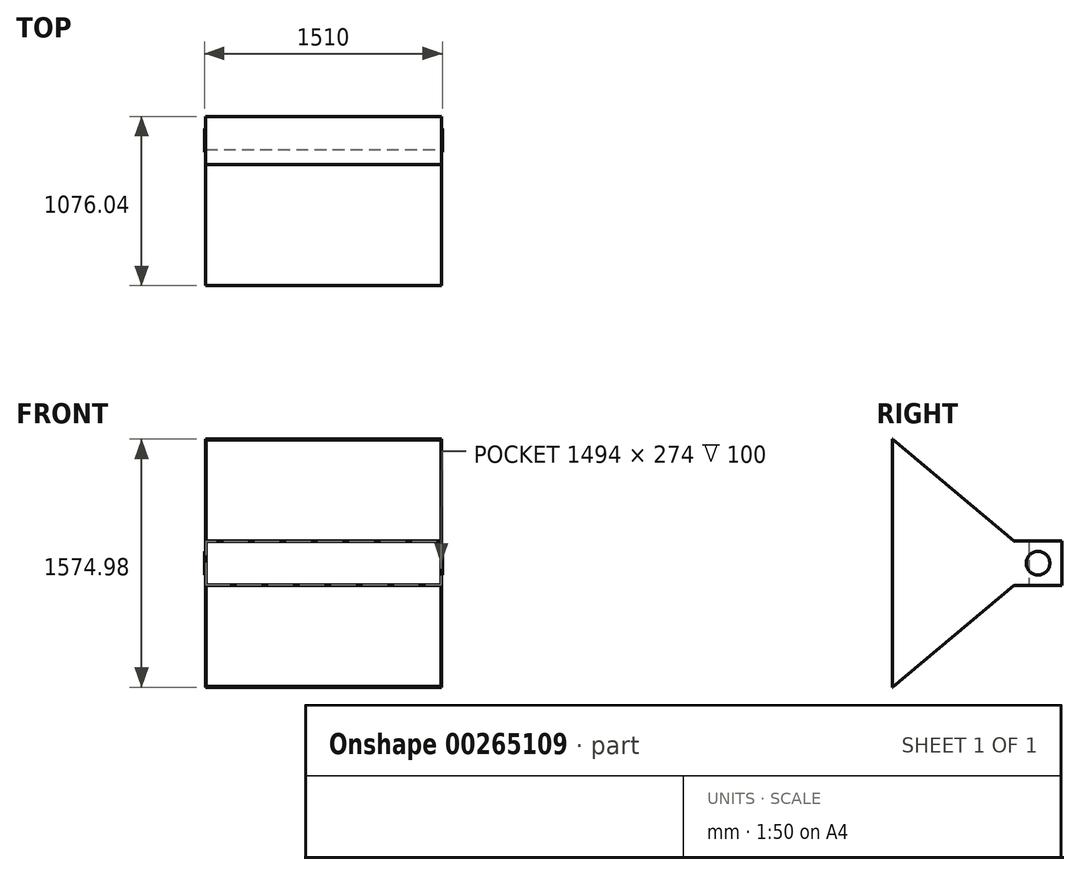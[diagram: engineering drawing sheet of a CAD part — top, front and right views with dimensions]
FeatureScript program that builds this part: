
annotation { "Feature Type Name" : "Feature", "Feature Type Description" : "" }
export const myFeature = defineFeature(function(context is Context, id is Id, definition is map)
    precondition{}
    {
        {
            var Q0;
            Q0=qCreatedBy(makeId("Front.planeOp"),FACE);
            var sketch = newSketch(context, id + "F0", { "sketchPlane" : qUnion([Q0])});
            skLineSegment(sketch, "E0.bottom", {"start": v(-750, 140) * mm, "end": v(750, 140) * mm});
            skLineSegment(sketch, "E0.top", {"start": v(-750, -140) * mm, "end": v(750, -140) * mm});
            skLineSegment(sketch, "E0.left", {"start": v(-750, 140) * mm, "end": v(-750, -140) * mm});
            skLineSegment(sketch, "E0.right", {"start": v(750, 140) * mm, "end": v(750, -140) * mm});
            skPoint(sketch, "E0.middle", {"position": v(0, 0) * mm});
            skSolve(sketch);
        }
        {
            var Q0;
            Q0 = qSketchRegion(id + "F0", true);
            extrude(context, id + "F1", {"entities" : qUnion([Q0]), "oppositeDirection" : true, "depth" : 210 * mm});
        }
        {
            var Q0;
            Q0=makeQuery(id+"F1.opExtrude","CAP_FACE",FACE,{"disambiguationData":[OSD([sQuery(id+"F0.wireOp",EDGE,"E0.bottom"),sQuery(id+"F0.wireOp",EDGE,"E0.top"),sQuery(id+"F0.wireOp",EDGE,"E0.left"),sQuery(id+"F0.wireOp",EDGE,"E0.right")])],"isStart":true});
            var sketch = newSketch(context, id + "F2", { "sketchPlane" : qUnion([Q0])});
            skLineSegment(sketch, "E1.bottom", {"start": v(-750, 140) * mm, "end": v(750, 140) * mm});
            skLineSegment(sketch, "E1.top", {"start": v(-750, -140) * mm, "end": v(750, -140) * mm});
            skLineSegment(sketch, "E1.left", {"start": v(-750, 140) * mm, "end": v(-750, -140) * mm});
            skLineSegment(sketch, "E1.right", {"start": v(750, 140) * mm, "end": v(750, -140) * mm});
            skPoint(sketch, "E1.middle", {"position": v(0, 0) * mm});
            skLineSegment(sketch, "E2.bottom", {"start": v(-747, 137) * mm, "end": v(747, 137) * mm});
            skLineSegment(sketch, "E2.top", {"start": v(-747, -137) * mm, "end": v(747, -137) * mm});
            skLineSegment(sketch, "E2.left", {"start": v(-747, 137) * mm, "end": v(-747, -137) * mm});
            skLineSegment(sketch, "E2.right", {"start": v(747, 137) * mm, "end": v(747, -137) * mm});
            skSolve(sketch);
        }
        {
            var Q0;
            Q0=makeQuery(id+"F2.imprint","IMPRINT",FACE,{"disambiguationData":[TD([[makeQuery(id+"F2.imprint","IMPRINT",EDGE,{"derivedFrom":sQuery(id+"F2.wireOp",EDGE,"E1.bottom")}),-1.0]])]});
            extrude(context, id + "F3", {"entities" : qUnion([Q0]), "operationType" : NewBodyOperationType.ADD, "depth" : 100 * mm});
        }
        {
            var Q0;
            Q0=makeQuery(id+"F3.boolean.opBoolean","MERGE",FACE,{"derivedFrom":[makeQuery(id+"F1.opExtrude","SWEPT_FACE",FACE,{"disambiguationData":[OSD([sQuery(id+"F0.wireOp",EDGE,"E0.right")])]}),makeQuery(id+"F3.opExtrude","SWEPT_FACE",FACE,{"disambiguationData":[OSD([sQuery(id+"F2.wireOp",EDGE,"E1.right")])]})]});
            var sketch = newSketch(context, id + "F4", { "sketchPlane" : qUnion([Q0])});
            skLineSegment(sketch, "E3", {"start": v(-100, 140) * mm, "end": v(-866.04, 782.79) * mm});
            skLineSegment(sketch, "E4", {"start": v(-866.04, 782.79) * mm, "end": v(-866.04, 787.49) * mm});
            skLineSegment(sketch, "E5", {"start": v(-866.04, 787.49) * mm, "end": v(-863.44, 787.49) * mm});
            skLineSegment(sketch, "E6", {"start": v(-863.44, 787.49) * mm, "end": v(-863.44, 784.75) * mm});
            skLineSegment(sketch, "E7", {"start": v(-863.44, 784.75) * mm, "end": v(-95.06, 140) * mm});
            skLineSegment(sketch, "E8", {"start": v(0, 0) * mm, "end": v(-196.26, 0) * mm});
            skLineSegment(sketch, "E9.MirrorCS", {"start": v(-863.44, -784.75) * mm, "end": v(-95.06, -140) * mm});
            skLineSegment(sketch, "E10.MirrorCS", {"start": v(-866.04, -782.79) * mm, "end": v(-866.04, -787.49) * mm});
            skLineSegment(sketch, "E11.MirrorCS", {"start": v(-866.04, -787.49) * mm, "end": v(-863.44, -787.49) * mm});
            skLineSegment(sketch, "E12.MirrorCS", {"start": v(-863.44, -787.49) * mm, "end": v(-863.44, -784.75) * mm});
            skLineSegment(sketch, "E13.MirrorCS", {"start": v(-100, -140) * mm, "end": v(-866.04, -782.79) * mm});
            skSolve(sketch);
        }
        {
            var Q0;
            {var subQ0=sQuery(id+"F4.wireOp",EDGE,"E3");Q0=makeQuery(id+"F4.imprint","IMPRINT",FACE,{"disambiguationData":[TD([[makeQuery(id+"F4.imprint","IMPRINT",EDGE,{"derivedFrom":subQ0}),-1.0]])]});}
            var Q1;
            {var subQ0=sQuery(id+"F4.wireOp",EDGE,"E9.MirrorCS");Q1=makeQuery(id+"F4.imprint","IMPRINT",FACE,{"disambiguationData":[TD([[makeQuery(id+"F4.imprint","IMPRINT",EDGE,{"derivedFrom":subQ0}),1.0]])]});}
            extrude(context, id + "F5", {"entities" : qUnion([Q0, Q1]), "operationType" : NewBodyOperationType.ADD, "oppositeDirection" : true, "depth" : 1500 * mm});
        }
        {
            var Q0;
            {var subQ0=sQuery(id+"F2.wireOp",EDGE,"E1.right");var subQ1=sQuery(id+"F0.wireOp",EDGE,"E0.right");Q0=makeQuery(id+"F5.boolean.opBoolean","MERGE",FACE,{"derivedFrom":[makeQuery(id+"F3.boolean.opBoolean","MERGE",FACE,{"derivedFrom":[makeQuery(id+"F1.opExtrude","SWEPT_FACE",FACE,{"disambiguationData":[OSD([subQ1])]}),makeQuery(id+"F3.opExtrude","SWEPT_FACE",FACE,{"disambiguationData":[OSD([subQ0])]})]}),makeQuery(id+"F5.opExtrude","CAP_FACE",FACE,{"disambiguationData":[OSD([sQuery(id+"F0.wireOp",EDGE,"E0.bottom"),subQ1,sQuery(id+"F2.wireOp",EDGE,"E1.bottom"),subQ0,sQuery(id+"F4.wireOp",EDGE,"E3"),sQuery(id+"F4.wireOp",EDGE,"E4"),sQuery(id+"F4.wireOp",EDGE,"E5"),sQuery(id+"F4.wireOp",EDGE,"E6"),sQuery(id+"F4.wireOp",EDGE,"E7")])],"isStart":true}),makeQuery(id+"F5.opExtrude","CAP_FACE",FACE,{"disambiguationData":[OSD([sQuery(id+"F0.wireOp",EDGE,"E0.top"),subQ1,sQuery(id+"F2.wireOp",EDGE,"E1.top"),subQ0,sQuery(id+"F4.wireOp",EDGE,"E9.MirrorCS"),sQuery(id+"F4.wireOp",EDGE,"E10.MirrorCS"),sQuery(id+"F4.wireOp",EDGE,"E11.MirrorCS"),sQuery(id+"F4.wireOp",EDGE,"E12.MirrorCS"),sQuery(id+"F4.wireOp",EDGE,"E13.MirrorCS")])],"isStart":true})]});}
            var sketch = newSketch(context, id + "F6", { "sketchPlane" : qUnion([Q0])});
            skCircle(sketch, "E14", {"center": v(57.47, 0) * mm, "radius": 75 * mm});
            skPoint(sketch, "E14.centerSnap0", {"position": v(57.47, -140) * mm});
            skPoint(sketch, "E14.centerSnap1", {"position": v(-100, 0) * mm});
            skSolve(sketch);
        }
        {
            var Q0;
            Q0 = qSketchRegion(id + "F6", true);
            var Q1;
            Q1=makeQuery(id+"F6.imprint","IMPRINT",FACE,{"disambiguationData":[TD([[makeQuery(id+"F6.imprint","IMPRINT",EDGE,{"derivedFrom":sQuery(id+"F6.wireOp",EDGE,"E14")}),1.0]])]});
            extrude(context, id + "F7", {"entities" : qUnion([Q0, Q1]), "operationType" : NewBodyOperationType.ADD, "depth" : 5 * mm});
        }
        {
            var Q0;
            {var subQ0=sQuery(id+"F2.wireOp",EDGE,"E1.right");var subQ1=sQuery(id+"F0.wireOp",EDGE,"E0.right");Q0=makeQuery(id+"F5.boolean.opBoolean","MERGE",FACE,{"derivedFrom":[makeQuery(id+"F3.boolean.opBoolean","MERGE",FACE,{"derivedFrom":[makeQuery(id+"F1.opExtrude","SWEPT_FACE",FACE,{"disambiguationData":[OSD([sQuery(id+"F0.wireOp",EDGE,"E0.left")])]}),makeQuery(id+"F3.opExtrude","SWEPT_FACE",FACE,{"disambiguationData":[OSD([sQuery(id+"F2.wireOp",EDGE,"E1.left")])]})]}),makeQuery(id+"F5.opExtrude","CAP_FACE",FACE,{"disambiguationData":[OSD([sQuery(id+"F0.wireOp",EDGE,"E0.bottom"),subQ1,sQuery(id+"F2.wireOp",EDGE,"E1.bottom"),subQ0,sQuery(id+"F4.wireOp",EDGE,"E3"),sQuery(id+"F4.wireOp",EDGE,"E4"),sQuery(id+"F4.wireOp",EDGE,"E5"),sQuery(id+"F4.wireOp",EDGE,"E6"),sQuery(id+"F4.wireOp",EDGE,"E7")])],"isStart":false}),makeQuery(id+"F5.opExtrude","CAP_FACE",FACE,{"disambiguationData":[OSD([sQuery(id+"F0.wireOp",EDGE,"E0.top"),subQ1,sQuery(id+"F2.wireOp",EDGE,"E1.top"),subQ0,sQuery(id+"F4.wireOp",EDGE,"E9.MirrorCS"),sQuery(id+"F4.wireOp",EDGE,"E10.MirrorCS"),sQuery(id+"F4.wireOp",EDGE,"E11.MirrorCS"),sQuery(id+"F4.wireOp",EDGE,"E12.MirrorCS"),sQuery(id+"F4.wireOp",EDGE,"E13.MirrorCS")])],"isStart":false})]});}
            var sketch = newSketch(context, id + "F8", { "sketchPlane" : qUnion([Q0])});
            skCircle(sketch, "E15", {"center": v(-57.47, 0) * mm, "radius": 75 * mm});
            skPoint(sketch, "E15.centerSnap0", {"position": v(-57.47, 140) * mm});
            skPoint(sketch, "E15.centerSnap1", {"position": v(100, 0) * mm});
            skSolve(sketch);
        }
        {
            var Q0;
            Q0 = qSketchRegion(id + "F8", true);
            extrude(context, id + "F9", {"entities" : qUnion([Q0]), "operationType" : NewBodyOperationType.ADD, "depth" : 5 * mm});
        }
        {
            var Q0;
            {var subQ0=sQuery(id+"F2.wireOp",EDGE,"E1.right");var subQ1=sQuery(id+"F0.wireOp",EDGE,"E0.right");Q0=makeQuery(id+"F5.boolean.opBoolean","MERGE",FACE,{"derivedFrom":[makeQuery(id+"F3.boolean.opBoolean","MERGE",FACE,{"derivedFrom":[makeQuery(id+"F1.opExtrude","SWEPT_FACE",FACE,{"disambiguationData":[OSD([sQuery(id+"F0.wireOp",EDGE,"E0.left")])]}),makeQuery(id+"F3.opExtrude","SWEPT_FACE",FACE,{"disambiguationData":[OSD([sQuery(id+"F2.wireOp",EDGE,"E1.left")])]})]}),makeQuery(id+"F5.opExtrude","CAP_FACE",FACE,{"disambiguationData":[OSD([sQuery(id+"F0.wireOp",EDGE,"E0.bottom"),subQ1,sQuery(id+"F2.wireOp",EDGE,"E1.bottom"),subQ0,sQuery(id+"F4.wireOp",EDGE,"E3"),sQuery(id+"F4.wireOp",EDGE,"E4"),sQuery(id+"F4.wireOp",EDGE,"E5"),sQuery(id+"F4.wireOp",EDGE,"E6"),sQuery(id+"F4.wireOp",EDGE,"E7")])],"isStart":false}),makeQuery(id+"F5.opExtrude","CAP_FACE",FACE,{"disambiguationData":[OSD([sQuery(id+"F0.wireOp",EDGE,"E0.top"),subQ1,sQuery(id+"F2.wireOp",EDGE,"E1.top"),subQ0,sQuery(id+"F4.wireOp",EDGE,"E9.MirrorCS"),sQuery(id+"F4.wireOp",EDGE,"E10.MirrorCS"),sQuery(id+"F4.wireOp",EDGE,"E11.MirrorCS"),sQuery(id+"F4.wireOp",EDGE,"E12.MirrorCS"),sQuery(id+"F4.wireOp",EDGE,"E13.MirrorCS")])],"isStart":false})]});}
            var sketch = newSketch(context, id + "F10", { "sketchPlane" : qUnion([Q0])});
            skLineSegment(sketch, "E16", {"start": v(863.44, 787.49) * mm, "end": v(866.04, 787.49) * mm});
            skLineSegment(sketch, "E17", {"start": v(866.04, 787.49) * mm, "end": v(866.04, 782.79) * mm});
            skLineSegment(sketch, "E18", {"start": v(866.04, 782.79) * mm, "end": v(866.04, -782.79) * mm});
            skLineSegment(sketch, "E19", {"start": v(866.04, -782.79) * mm, "end": v(866.04, -787.49) * mm});
            skLineSegment(sketch, "E20", {"start": v(866.04, -787.49) * mm, "end": v(863.44, -787.49) * mm});
            skLineSegment(sketch, "E21", {"start": v(863.44, -787.49) * mm, "end": v(863.44, -784.75) * mm});
            skLineSegment(sketch, "E22", {"start": v(863.44, -784.75) * mm, "end": v(95.06, -140) * mm});
            skLineSegment(sketch, "E23", {"start": v(95.06, -140) * mm, "end": v(100, -140) * mm});
            skLineSegment(sketch, "E24", {"start": v(100, -140) * mm, "end": v(100, 140) * mm});
            skLineSegment(sketch, "E25", {"start": v(100, 140) * mm, "end": v(95.06, 140) * mm});
            skLineSegment(sketch, "E26", {"start": v(95.06, 140) * mm, "end": v(863.44, 784.75) * mm});
            skLineSegment(sketch, "E27", {"start": v(863.44, 784.75) * mm, "end": v(863.44, 787.49) * mm});
            skSolve(sketch);
        }
        {
            var Q0;
            Q0=makeQuery(id+"F10.imprint","IMPRINT",FACE,{"disambiguationData":[TD([[makeQuery(id+"F10.imprint","IMPRINT",EDGE,{"derivedFrom":sQuery(id+"F10.wireOp",EDGE,"E18")}),-1.0]])]});
            var Q1;
            Q1=makeQuery(id+"F10.imprint","IMPRINT",FACE,{"disambiguationData":[TD([[makeQuery(id+"F10.imprint","IMPRINT",EDGE,{"derivedFrom":sQuery(id+"F10.wireOp",EDGE,"E16")}),1.0]])]});
            var Q2;
            Q2=makeQuery(id+"F10.imprint","IMPRINT",FACE,{"disambiguationData":[TD([[makeQuery(id+"F10.imprint","IMPRINT",EDGE,{"derivedFrom":sQuery(id+"F10.wireOp",EDGE,"E19")}),-1.0]])]});
            extrude(context, id + "F11", {"entities" : qUnion([Q0, Q1, Q2]), "operationType" : NewBodyOperationType.ADD, "oppositeDirection" : true, "depth" : 3 * mm});
        }
        {
            var Q0;
            {var subQ0=sQuery(id+"F2.wireOp",EDGE,"E1.right");var subQ1=sQuery(id+"F0.wireOp",EDGE,"E0.right");Q0=makeQuery(id+"F5.boolean.opBoolean","MERGE",FACE,{"derivedFrom":[makeQuery(id+"F3.boolean.opBoolean","MERGE",FACE,{"derivedFrom":[makeQuery(id+"F1.opExtrude","SWEPT_FACE",FACE,{"disambiguationData":[OSD([subQ1])]}),makeQuery(id+"F3.opExtrude","SWEPT_FACE",FACE,{"disambiguationData":[OSD([subQ0])]})]}),makeQuery(id+"F5.opExtrude","CAP_FACE",FACE,{"disambiguationData":[OSD([sQuery(id+"F0.wireOp",EDGE,"E0.bottom"),subQ1,sQuery(id+"F2.wireOp",EDGE,"E1.bottom"),subQ0,sQuery(id+"F4.wireOp",EDGE,"E3"),sQuery(id+"F4.wireOp",EDGE,"E4"),sQuery(id+"F4.wireOp",EDGE,"E5"),sQuery(id+"F4.wireOp",EDGE,"E6"),sQuery(id+"F4.wireOp",EDGE,"E7")])],"isStart":true}),makeQuery(id+"F5.opExtrude","CAP_FACE",FACE,{"disambiguationData":[OSD([sQuery(id+"F0.wireOp",EDGE,"E0.top"),subQ1,sQuery(id+"F2.wireOp",EDGE,"E1.top"),subQ0,sQuery(id+"F4.wireOp",EDGE,"E9.MirrorCS"),sQuery(id+"F4.wireOp",EDGE,"E10.MirrorCS"),sQuery(id+"F4.wireOp",EDGE,"E11.MirrorCS"),sQuery(id+"F4.wireOp",EDGE,"E12.MirrorCS"),sQuery(id+"F4.wireOp",EDGE,"E13.MirrorCS")])],"isStart":true})]});}
            var sketch = newSketch(context, id + "F12", { "sketchPlane" : qUnion([Q0])});
            skLineSegment(sketch, "E28", {"start": v(-866.04, -787.49) * mm, "end": v(-863.44, -787.49) * mm});
            skLineSegment(sketch, "E29", {"start": v(-863.44, -787.49) * mm, "end": v(-863.44, -784.75) * mm});
            skLineSegment(sketch, "E30", {"start": v(-863.44, -784.75) * mm, "end": v(-95.06, -140) * mm});
            skLineSegment(sketch, "E31", {"start": v(-95.06, -140) * mm, "end": v(-100, -140) * mm});
            skLineSegment(sketch, "E32", {"start": v(-100, -140) * mm, "end": v(-100, 140) * mm});
            skLineSegment(sketch, "E33", {"start": v(-100, 140) * mm, "end": v(-95.06, 140) * mm});
            skLineSegment(sketch, "E34", {"start": v(-95.06, 140) * mm, "end": v(-863.44, 784.75) * mm});
            skLineSegment(sketch, "E35", {"start": v(-863.44, 784.75) * mm, "end": v(-863.44, 787.49) * mm});
            skLineSegment(sketch, "E36", {"start": v(-863.44, 787.49) * mm, "end": v(-866.04, 787.49) * mm});
            skLineSegment(sketch, "E37", {"start": v(-866.04, 787.49) * mm, "end": v(-866.04, 782.79) * mm});
            skLineSegment(sketch, "E38", {"start": v(-866.04, 782.79) * mm, "end": v(-866.04, -782.79) * mm});
            skLineSegment(sketch, "E39", {"start": v(-866.04, -782.79) * mm, "end": v(-866.04, -787.49) * mm});
            skSolve(sketch);
        }
        {
            var Q0;
            Q0=makeQuery(id+"F12.imprint","IMPRINT",FACE,{"disambiguationData":[TD([[makeQuery(id+"F12.imprint","IMPRINT",EDGE,{"derivedFrom":sQuery(id+"F12.wireOp",EDGE,"E32")}),-1.0]])]});
            var Q1;
            Q1=makeQuery(id+"F12.imprint","IMPRINT",FACE,{"disambiguationData":[TD([[makeQuery(id+"F12.imprint","IMPRINT",EDGE,{"derivedFrom":sQuery(id+"F12.wireOp",EDGE,"E28")}),1.0]])]});
            extrude(context, id + "F13", {"entities" : qUnion([Q0, Q1]), "operationType" : NewBodyOperationType.ADD, "oppositeDirection" : true, "depth" : 3 * mm});
        }
    });
